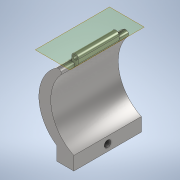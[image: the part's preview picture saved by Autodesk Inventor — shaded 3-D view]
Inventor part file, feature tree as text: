
AUTODESK INVENTOR PART (.ipt)
format: ipt  version: 2021 (Build 250183000, 183)  size: 181,248 bytes
history: native  units: in
note: dims shown in document units (in); Inventor stores cm internally (conversion verified against a paired STEP export)
features: sketch x6, extrude x5, fillet x3, plane x1, hole x1
ambient origin geometry x8: Origin, YZ Plane, XZ Plane, XY Plane, X Axis, Y Axis, Z Axis, Center Point
bodies: Solid1 (feature_tree)
feature tree (16):
  extrude  "Extrusion1"  Depth=3.937in TaperAngle=0.0deg
  extrude  "Extrusion2"  Depth=0.1969in
  plane  "Work Plane1"
  extrude  "Extrusion3"  Depth=3.937in TaperAngle=0.0deg
  extrude  "Extrusion4"  Depth=0.7874in
  extrude  "Extrusion5"  Depth=0.4724in
  hole  "Hole1"  [1 undecoded]
  fillet  "Fillet1"  Radius=0.3937in
  fillet  "Fillet2"  Radius=0.1181in
  fillet  "Fillet3"  Radius=0.9843in
  sketch  "Sketch1"  dims[d1=3.937in d2=2.3622in d3=0.7874in d5=0.4724in d6=3.937in d7=1.1811in d8=0.3937in d9=3.937in d10=0.0in]
  sketch  "Sketch2"  dims[d11=0.2756in d12=0.1969in]
  sketch  "Sketch3"  dims[d13=0.3937in d14=3.937in d15=0.0in]
  sketch  "Sketch4"  dims[d17=0.4724in d18=0.0in d19=0.7874in]
  sketch  "Sketch5"  dims[d20=0.4724in d21=0.0in d22=0.2756in]
  sketch  "Sketch6"  dims[d23=2.3622in d24=0.0in d25=0.3937in d26=0.3937in d27=0.3937in d28=0.2362in d29=0.1575in d30=0.0787in d31=90.0deg d32=0.315in d33=0.8108in d34=0.1181in d35=0.9843in d37=2.3622in d39=0.1575in d40=0.1181in d41=0.7874in d42=0.0197in d43=0.0344in d44=0.0197in d45=0.0344in]
note: 1 required parameter value undecoded (feature->parameter linkage not recoverable at this tier; creation-order binding heuristic only, values carry confidence <= 0.55)
